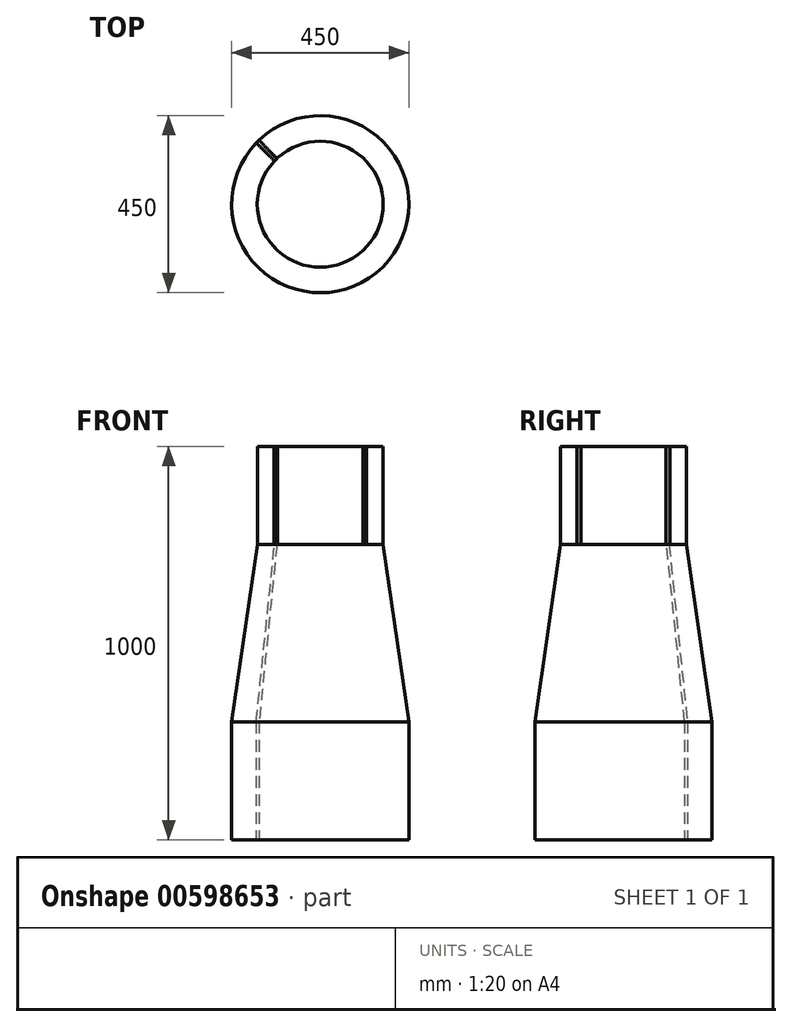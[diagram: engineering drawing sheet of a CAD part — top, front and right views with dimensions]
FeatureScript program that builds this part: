
annotation { "Feature Type Name" : "Feature", "Feature Type Description" : "" }
export const myFeature = defineFeature(function(context is Context, id is Id, definition is map)
    precondition{}
    {
        {
            var Q0;
            Q0=qCreatedBy(makeId("Top.planeOp"),FACE);
            var sketch = newSketch(context, id + "F0", { "sketchPlane" : qUnion([Q0])});
            skArc(sketch, "E0", {"start": v(-118.03, 108.03) * mm, "mid": v(-160, 0) * mm, "end": v(-118.03, -108.03) * mm});
            skLineSegment(sketch, "E1", {"start": v(-108.03, 118.03) * mm, "end": v(-118.03, 108.03) * mm});
            skLineSegment(sketch, "E2.1.0", {"start": v(-118.03, -108.03) * mm, "end": v(-108.03, -118.03) * mm});
            skLineSegment(sketch, "E2.2.0", {"start": v(108.03, -118.03) * mm, "end": v(118.03, -108.03) * mm});
            skLineSegment(sketch, "E2.3.0", {"start": v(118.03, 108.03) * mm, "end": v(108.03, 118.03) * mm});
            skArc(sketch, "E3.trimOffspring", {"start": v(108.03, 118.03) * mm, "mid": v(0, 160) * mm, "end": v(-108.03, 118.03) * mm});
            skArc(sketch, "E4.trimOffspring", {"start": v(118.03, -108.03) * mm, "mid": v(160, 0) * mm, "end": v(118.03, 108.03) * mm});
            skArc(sketch, "E5.trimOffspring", {"start": v(-108.03, -118.03) * mm, "mid": v(0, -160) * mm, "end": v(108.03, -118.03) * mm});
            skLineSegment(sketch, "E6", {"start": v(0, 0) * mm, "end": v(-159.1, 159.1) * mm, "construction": true});
            skLineSegment(sketch, "E7", {"start": v(0, 0) * mm, "end": v(-161.75, 0) * mm, "construction": true});
            skArc(sketch, "E8", {"start": v(-162.6, 155.52) * mm, "mid": v(159.1, -159.1) * mm, "end": v(-155.52, 162.6) * mm});
            skLineSegment(sketch, "E9", {"start": v(-155.52, 162.6) * mm, "end": v(-162.6, 155.52) * mm});
            skSolve(sketch);
        }
        {
            var Q0;
            Q0=makeQuery(id+"F0.imprint","IMPRINT",FACE,{"disambiguationData":[TD([[makeQuery(id+"F0.imprint","IMPRINT",EDGE,{"derivedFrom":sQuery(id+"F0.wireOp",EDGE,"E0")}),1.0]])]});
            extrude(context, id + "F1", {"entities" : qUnion([Q0]), "depth" : 1000 * mm, "offsetDistance" : 25 * mm});
        }
        {
            var Q0;
            Q0=makeQuery(id+"F0.imprint","IMPRINT",FACE,{"disambiguationData":[TD([[makeQuery(id+"F0.imprint","IMPRINT",EDGE,{"derivedFrom":sQuery(id+"F0.wireOp",EDGE,"E0")}),-1.0]])]});
            extrude(context, id + "F2", {"entities" : qUnion([Q0]), "operationType" : NewBodyOperationType.ADD, "depth" : 750 * mm, "offsetDistance" : 25 * mm});
        }
        {
            var Q0;
            Q0=makeQuery(id+"F2.opExtrude","CAP_EDGE",EDGE,{"disambiguationData":[OSD([sQuery(id+"F0.wireOp",EDGE,"E9")])],"isStart":false});
            var Q1;
            Q1=makeQuery(id+"F2.opExtrude","CAP_EDGE",EDGE,{"disambiguationData":[OSD([sQuery(id+"F0.wireOp",EDGE,"E8")])],"isStart":false});
            chamfer(context, id + "F3", {"entities" : qUnion([Q0, Q1]), "chamferType" : ChamferType.TWO_OFFSETS, "width1" : 65 * mm, "oppositeDirection" : false, "width2" : 450 * mm, "tangentPropagation" : true});
        }
    });
